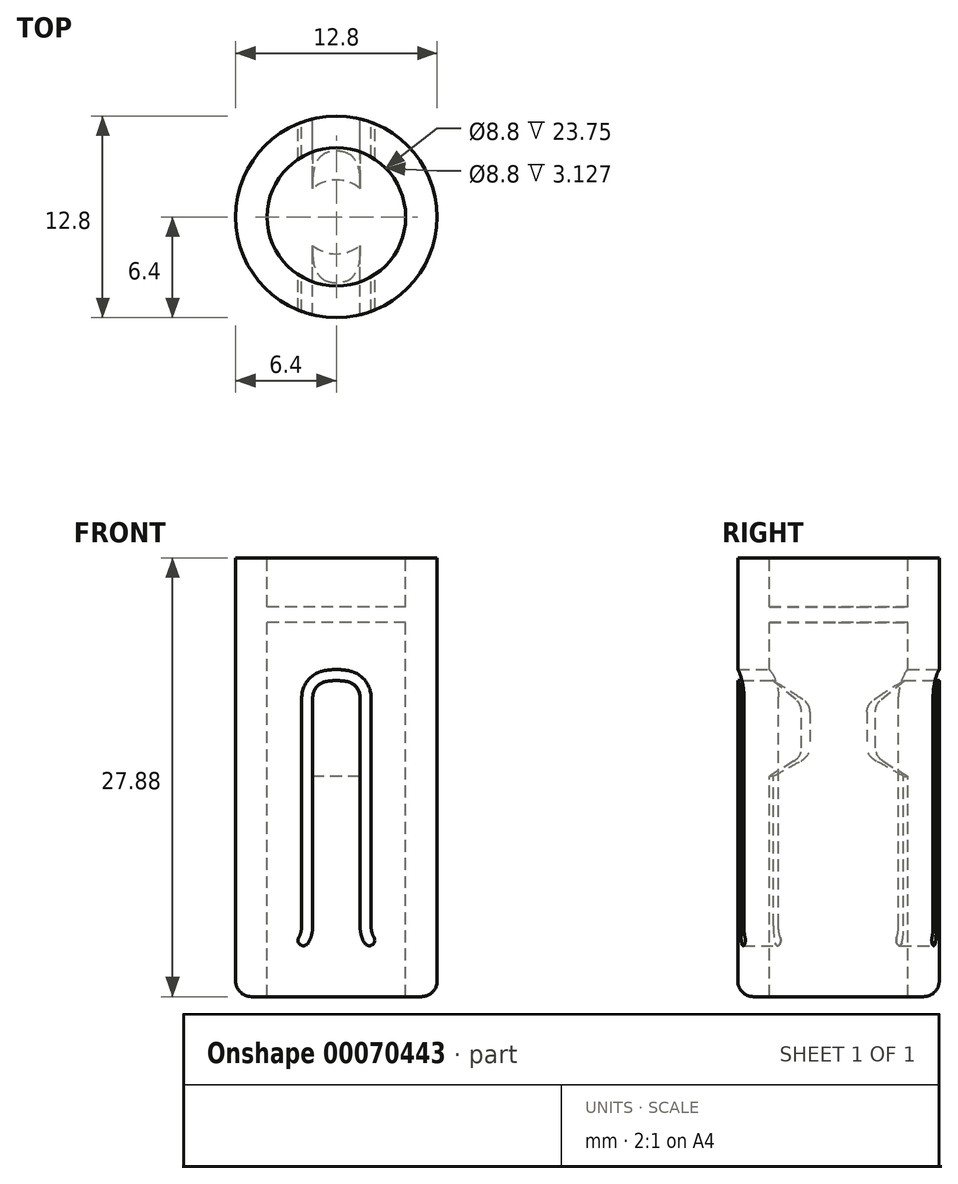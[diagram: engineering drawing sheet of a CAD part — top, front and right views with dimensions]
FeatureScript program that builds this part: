
annotation { "Feature Type Name" : "Feature", "Feature Type Description" : "" }
export const myFeature = defineFeature(function(context is Context, id is Id, definition is map)
    precondition{}
    {
        {
            var Q0;
            Q0=qCreatedBy(makeId("Front.planeOp"),FACE);
            var sketch = newSketch(context, id + "F0", { "sketchPlane" : qUnion([Q0])});
            skLineSegment(sketch, "E0", {"start": v(0, 47.32) * mm, "end": v(0, -47.32) * mm, "construction": true});
            skPoint(sketch, "E1", {"position": v(0, 0) * mm});
            skPoint(sketch, "E2", {"position": v(0, -24.6) * mm});
            skLineSegment(sketch, "E3", {"start": v(4.4, -42.36) * mm, "end": v(4.4, -28.36) * mm});
            skLineSegment(sketch, "E4", {"start": v(4.4, -22.1) * mm, "end": v(4.4, -18.6) * mm});
            skLineSegment(sketch, "E5", {"start": v(4.4, -18.6) * mm, "end": v(0, -18.6) * mm});
            skLineSegment(sketch, "E6", {"start": v(5.4, -42.36) * mm, "end": v(4.4, -42.36) * mm});
            skLineSegment(sketch, "E7", {"start": v(6.4, -41.36) * mm, "end": v(6.4, -14.48) * mm});
            skLineSegment(sketch, "E8", {"start": v(4.4, -22.1) * mm, "end": v(2.72, -23.49) * mm});
            skLineSegment(sketch, "E9", {"start": v(2.35, -24.26) * mm, "end": v(2.35, -26.55) * mm});
            skLineSegment(sketch, "E10", {"start": v(2.83, -27.4) * mm, "end": v(4.4, -28.36) * mm});
            skLineSegment(sketch, "E11", {"start": v(0, -17.6) * mm, "end": v(4.4, -17.6) * mm});
            skLineSegment(sketch, "E12", {"start": v(4.4, -17.6) * mm, "end": v(4.4, -14.48) * mm});
            skLineSegment(sketch, "E13", {"start": v(4.4, -14.48) * mm, "end": v(6.4, -14.48) * mm});
            skLineSegment(sketch, "E14", {"start": v(0, -17.6) * mm, "end": v(0, -18.6) * mm});
            skPoint(sketch, "E15.visualSharp", {"position": v(2.35, -23.79) * mm});
            skArc(sketch, "E15.filletArc", {"start": v(2.72, -23.49) * mm, "mid": v(2.45, -23.83) * mm, "end": v(2.35, -24.26) * mm});
            skPoint(sketch, "E16.visualSharp", {"position": v(2.35, -27.1) * mm});
            skArc(sketch, "E16.filletArc", {"start": v(2.35, -26.55) * mm, "mid": v(2.48, -27.04) * mm, "end": v(2.83, -27.4) * mm});
            skPoint(sketch, "E17.visualSharp", {"position": v(6.4, -42.36) * mm});
            skArc(sketch, "E17.filletArc", {"start": v(5.4, -42.36) * mm, "mid": v(6.1, -42.06) * mm, "end": v(6.4, -41.36) * mm});
            skSolve(sketch);
        }
        {
            var Q0;
            Q0=makeQuery(id+"F0.imprint","IMPRINT",FACE,{"disambiguationData":[TD([[makeQuery(id+"F0.imprint","IMPRINT",EDGE,{"derivedFrom":sQuery(id+"F0.wireOp",EDGE,"E3")}),-1.0]])]});
            var Q1;
            Q1=sQuery(id+"F0.wireOp",EDGE,"E0");
            revolve(context, id + "F1", {"entities" : qUnion([Q0]), "axis" : qUnion([Q1]), "revolveType" : RevolveType.FULL});
        }
        {
            var Q0;
            Q0=makeQuery(id+"F1.opRevolve","SWEPT_FACE",FACE,{"disambiguationData":[OSD([sQuery(id+"F0.wireOp",EDGE,"E6")])]});
            cPlane(context, id + "F2", {"entities" : qUnion([Q0]), "cplaneType" : CPlaneType.OFFSET, "offset" : 0 * mm, "width" : 150 * mm, "height" : 150 * mm});
        }
        {
            var Q0;
            Q0=qCreatedBy(id+"F2.planeOp",FACE);
            var sketch = newSketch(context, id + "F3", { "sketchPlane" : qUnion([Q0])});
            skLineSegment(sketch, "E18", {"start": v(0, 8.07) * mm, "end": v(0, -8.07) * mm, "construction": true});
            skLineSegment(sketch, "E19", {"start": v(-9.24, 0) * mm, "end": v(9.24, 0) * mm, "construction": true});
            skPoint(sketch, "E20", {"position": v(0, 0) * mm});
            skCircle(sketch, "E21", {"center": v(0, 0) * mm, "radius": 4.4 * mm});
            skCircle(sketch, "E22", {"center": v(0, 0) * mm, "radius": 2.35 * mm});
            skLineSegment(sketch, "E23", {"start": v(-1.5, -1.8) * mm, "end": v(-1.5, -4.14) * mm});
            skLineSegment(sketch, "E24.MirrorCS", {"start": v(1.5, -1.8) * mm, "end": v(1.5, -4.14) * mm});
            skLineSegment(sketch, "E25.MirrorCS", {"start": v(-1.5, 1.8) * mm, "end": v(-1.5, 4.14) * mm});
            skLineSegment(sketch, "E26.MirrorCS", {"start": v(1.5, 1.8) * mm, "end": v(1.5, 4.14) * mm});
            skSolve(sketch);
        }
        {
            var Q0;
            {var subQ0=sQuery(id+"F3.wireOp",EDGE,"E23");Q0=makeQuery(id+"F3.imprint","IMPRINT",FACE,{"disambiguationData":[TD([[makeQuery(id+"F3.imprint","IMPRINT",EDGE,{"derivedFrom":subQ0}),-1.0]])]});}
            var Q1;
            {var subQ0=sQuery(id+"F3.wireOp",EDGE,"E24.MirrorCS");Q1=makeQuery(id+"F3.imprint","IMPRINT",FACE,{"disambiguationData":[TD([[makeQuery(id+"F3.imprint","IMPRINT",EDGE,{"derivedFrom":subQ0}),1.0]])]});}
            extrude(context, id + "F4", {"entities" : qUnion([Q0, Q1]), "operationType" : NewBodyOperationType.REMOVE, "oppositeDirection" : true, "depth" : 23.35 * mm});
        }
        {
            var Q0;
            Q0=qCreatedBy(makeId("Front.planeOp"),FACE);
            cPlane(context, id + "F5", {"entities" : qUnion([Q0]), "cplaneType" : CPlaneType.OFFSET, "offset" : 6.4 * mm, "oppositeDirection" : true, "width" : 150 * mm, "height" : 150 * mm});
        }
        {
            var Q0;
            Q0=qCreatedBy(id+"F5.planeOp",FACE);
            var sketch = newSketch(context, id + "F6", { "sketchPlane" : qUnion([Q0])});
            skLineSegment(sketch, "E27", {"start": v(1.5, -37.85) * mm, "end": v(1.5, -23.33) * mm});
            skArc(sketch, "E28", {"start": v(0, -22.28) * mm, "mid": v(0.35, -22.3) * mm, "end": v(0.7, -22.35) * mm});
            skPoint(sketch, "E28.startSnap0", {"position": v(0.02, -22.28) * mm});
            skPoint(sketch, "E29.visualSharp", {"position": v(1.5, -22.61) * mm});
            skArc(sketch, "E29.filletArc", {"start": v(1.5, -23.33) * mm, "mid": v(1.27, -22.7) * mm, "end": v(0.7, -22.35) * mm});
            skArc(sketch, "E30", {"start": v(1.5, -37.85) * mm, "mid": v(1.57, -38.42) * mm, "end": v(1.78, -38.95) * mm});
            skPoint(sketch, "E31.orphan", {"position": v(1.5, -39.36) * mm});
            skArc(sketch, "E32.MirrorCS", {"start": v(-1.5, -37.85) * mm, "mid": v(-1.57, -38.42) * mm, "end": v(-1.78, -38.95) * mm});
            skLineSegment(sketch, "E33.MirrorCS", {"start": v(-1.5, -37.85) * mm, "end": v(-1.5, -23.33) * mm});
            skArc(sketch, "E34.MirrorCS", {"start": v(-1.5, -23.33) * mm, "mid": v(-1.27, -22.7) * mm, "end": v(-0.7, -22.35) * mm});
            skArc(sketch, "E35.MirrorCS", {"start": v(0, -22.28) * mm, "mid": v(-0.35, -22.3) * mm, "end": v(-0.7, -22.35) * mm});
            skLineSegment(sketch, "E36.0", {"start": v(2.2, -37.85) * mm, "end": v(2.2, -23.33) * mm});
            skArc(sketch, "E37.0", {"start": v(2.2, -37.85) * mm, "mid": v(2.25, -38.24) * mm, "end": v(2.4, -38.6) * mm});
            skArc(sketch, "E38.0", {"start": v(2.2, -23.33) * mm, "mid": v(1.81, -22.25) * mm, "end": v(0.83, -21.66) * mm});
            skArc(sketch, "E39.0", {"start": v(0, -21.58) * mm, "mid": v(0.42, -21.6) * mm, "end": v(0.83, -21.66) * mm});
            skArc(sketch, "E40.MirrorCS", {"start": v(0, -21.58) * mm, "mid": v(-0.42, -21.6) * mm, "end": v(-0.83, -21.66) * mm});
            skArc(sketch, "E41.MirrorCS", {"start": v(-2.2, -23.33) * mm, "mid": v(-1.81, -22.25) * mm, "end": v(-0.83, -21.66) * mm});
            skLineSegment(sketch, "E42.MirrorCS", {"start": v(-2.2, -37.85) * mm, "end": v(-2.2, -23.33) * mm});
            skArc(sketch, "E43.MirrorCS", {"start": v(-2.2, -37.85) * mm, "mid": v(-2.25, -38.24) * mm, "end": v(-2.4, -38.6) * mm});
            skArc(sketch, "E44", {"start": v(-2.4, -38.6) * mm, "mid": v(-2.26, -39.08) * mm, "end": v(-1.78, -38.95) * mm});
            skPoint(sketch, "E44.centerSnap0", {"position": v(-2.5, -38.78) * mm});
            skPoint(sketch, "E45.orphan", {"position": v(-2.1, -39.4) * mm});
            skPoint(sketch, "E46.orphan", {"position": v(-3.3, -39.34) * mm});
            skArc(sketch, "E47.MirrorCS", {"start": v(2.4, -38.6) * mm, "mid": v(2.26, -39.08) * mm, "end": v(1.78, -38.95) * mm});
            skPoint(sketch, "E48.orphan", {"position": v(3.3, -39.34) * mm});
            skPoint(sketch, "E49.orphan", {"position": v(2.1, -39.4) * mm});
            skSolve(sketch);
        }
        {
            var Q0;
            Q0 = qSketchRegion(id + "F6", true);
            extrude(context, id + "F7", {"entities" : qUnion([Q0]), "operationType" : NewBodyOperationType.REMOVE, "depth" : 12.8 * mm});
        }
    });
